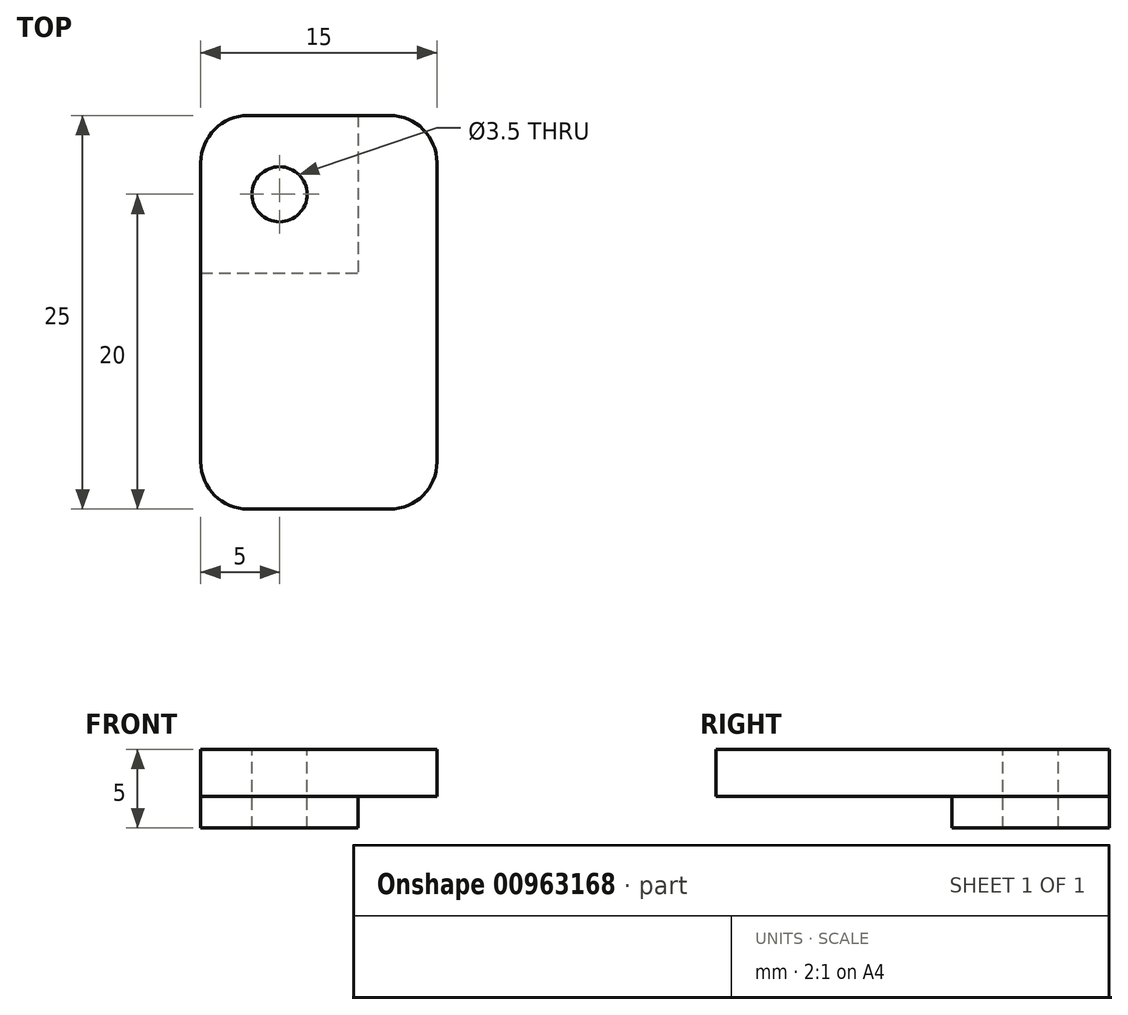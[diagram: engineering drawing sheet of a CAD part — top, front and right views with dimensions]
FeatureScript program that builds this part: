
annotation { "Feature Type Name" : "Feature", "Feature Type Description" : "" }
export const myFeature = defineFeature(function(context is Context, id is Id, definition is map)
    precondition{}
    {
        {
            var Q0;
            Q0=qCreatedBy(makeId("Top.planeOp"),FACE);
            var sketch = newSketch(context, id + "F0", { "sketchPlane" : qUnion([Q0])});
            skLineSegment(sketch, "E0.bottom", {"start": v(0, 0) * mm, "end": v(15, 0) * mm});
            skLineSegment(sketch, "E0.top", {"start": v(0, -25) * mm, "end": v(15, -25) * mm});
            skLineSegment(sketch, "E0.left", {"start": v(0, 0) * mm, "end": v(0, -25) * mm});
            skLineSegment(sketch, "E0.right", {"start": v(15, 0) * mm, "end": v(15, -25) * mm});
            skPoint(sketch, "E1", {"position": v(5, -5) * mm});
            skSolve(sketch);
        }
        {
            var Q0;
            Q0=makeQuery(id+"F0.imprint","IMPRINT",FACE,{"disambiguationData":[TD([[makeQuery(id+"F0.imprint","IMPRINT",EDGE,{"derivedFrom":sQuery(id+"F0.wireOp",EDGE,"E0.bottom")}),-1.0]])]});
            extrude(context, id + "F1", {"entities" : qUnion([Q0]), "depth" : 3 * mm, "offsetDistance" : 25 * mm});
        }
        {
            var Q0;
            Q0=makeQuery(id+"F1.opExtrude","CAP_FACE",FACE,{"disambiguationData":[OSD([sQuery(id+"F0.wireOp",EDGE,"E0.bottom"),sQuery(id+"F0.wireOp",EDGE,"E0.top"),sQuery(id+"F0.wireOp",EDGE,"E0.left"),sQuery(id+"F0.wireOp",EDGE,"E0.right")])],"isStart":true});
            var sketch = newSketch(context, id + "F2", { "sketchPlane" : qUnion([Q0])});
            skLineSegment(sketch, "E2.bottom", {"start": v(0, 0) * mm, "end": v(10, 0) * mm});
            skLineSegment(sketch, "E2.top", {"start": v(0, 10) * mm, "end": v(10, 10) * mm});
            skLineSegment(sketch, "E2.left", {"start": v(0, 0) * mm, "end": v(0, 10) * mm});
            skLineSegment(sketch, "E2.right", {"start": v(10, 0) * mm, "end": v(10, 10) * mm});
            skSolve(sketch);
        }
        {
            var Q0;
            Q0=makeQuery(id+"F2.imprint","IMPRINT",FACE,{"disambiguationData":[TD([[makeQuery(id+"F2.imprint","IMPRINT",EDGE,{"derivedFrom":sQuery(id+"F2.wireOp",EDGE,"E2.bottom")}),1.0]])]});
            extrude(context, id + "F3", {"entities" : qUnion([Q0]), "operationType" : NewBodyOperationType.ADD, "depth" : 2 * mm, "offsetDistance" : 25 * mm});
        }
        {
            var Q0;
            Q0=makeQuery(id+"F3.boolean.opBoolean","MERGE",EDGE,{"derivedFrom":[makeQuery(id+"F1.opExtrude","SWEPT_EDGE",EDGE,{"disambiguationData":[OSD([sQuery(id+"F0.wireOp",EDGE,"E0.bottom"),sQuery(id+"F0.wireOp",EDGE,"E0.left")])]}),makeQuery(id+"F3.opExtrude","SWEPT_EDGE",EDGE,{"disambiguationData":[OSD([sQuery(id+"F2.wireOp",EDGE,"E2.bottom"),sQuery(id+"F2.wireOp",EDGE,"E2.left")])]})]});
            var Q1;
            Q1=makeQuery(id+"F1.opExtrude","SWEPT_EDGE",EDGE,{"disambiguationData":[OSD([sQuery(id+"F0.wireOp",EDGE,"E0.top"),sQuery(id+"F0.wireOp",EDGE,"E0.left")])]});
            var Q2;
            Q2=makeQuery(id+"F1.opExtrude","SWEPT_EDGE",EDGE,{"disambiguationData":[OSD([sQuery(id+"F0.wireOp",EDGE,"E0.top"),sQuery(id+"F0.wireOp",EDGE,"E0.right")])]});
            var Q3;
            Q3=makeQuery(id+"F1.opExtrude","SWEPT_EDGE",EDGE,{"disambiguationData":[OSD([sQuery(id+"F0.wireOp",EDGE,"E0.bottom"),sQuery(id+"F0.wireOp",EDGE,"E0.right")])]});
            fillet(context, id + "F4", {"entities" : qUnion([Q0, Q1, Q2, Q3]), "radius" : 3 * mm, "tangentPropagation" : true, "allowEdgeOverflow" : false});
        }
        {
            var Q0;
            Q0=makeQuery(id+"F1.opExtrude","CAP_FACE",FACE,{"disambiguationData":[OSD([sQuery(id+"F0.wireOp",EDGE,"E0.bottom"),sQuery(id+"F0.wireOp",EDGE,"E0.top"),sQuery(id+"F0.wireOp",EDGE,"E0.left"),sQuery(id+"F0.wireOp",EDGE,"E0.right")])],"isStart":false});
            var sketch = newSketch(context, id + "F5", { "sketchPlane" : qUnion([Q0])});
            skPoint(sketch, "E3.0", {"position": v(5, -5) * mm});
            skSolve(sketch);
        }
        {
            var Q0;
            Q0=sQuery(id+"F5.wireOp",VERTEX,"E3.0");
            var Q1;
            Q1=makeQuery(id+"F1.opExtrude","SWEPT_BODY",BODY,{"disambiguationData":[OSD([sQuery(id+"F0.wireOp",EDGE,"E0.bottom"),sQuery(id+"F0.wireOp",EDGE,"E0.top"),sQuery(id+"F0.wireOp",EDGE,"E0.left"),sQuery(id+"F0.wireOp",EDGE,"E0.right")])]});
            hole(context, id + "F6", {"style" : HoleStyle.SIMPLE, "endStyle" : HoleEndStyle.THROUGH, "holeDiameter" : 3.5 * mm, "majorDiameter" : 5 * mm, "tappedDepth" : 12 * mm, "tapClearance" : 3, "locations" : qUnion([Q0]), "scope" : qUnion([Q1])});
        }
    });
